# Revit family: BE_84840_de_DE
name_source: partatom
category: Leuchten
units: mm (PartAtom-declared; Revit-internal decimal feet)

## family parameters
Basisbauteil = Fläche
Beim Laden mit Abzugskörper schneiden = Ja
Bemaßung runder Anschluss = Durchmesser verwenden
Gemeinsam genutzt = Nein
Lichtquelle = Nein
Raumberechnungspunkt = Ja
Teiletyp = Normal

## types (2) — shared parameters
AC/DC = AC
Aktualisierung = 2022-05-19T04:00:07
Anschlussleitung = 5.0 m X05RN-F FEP 2 × 1² + 1G2,5²
BEGA_Dummy = Nein
BEGA_Intern = Ja
BEGA_Intern_Konstruktion = Ja
BEGA_Intern_an = Ja
BEGA_Intern_aus = Ja
Beschreibung = Flächenscheinwerfer BEGA UniLink
Beschreibung_Sonderanfertigung = Hier können Sie Informationen zur Sonderanfertigung eintragen.
CE_Konformität = ja
Energieeffizienzklasse = LED A++ - A
Farbwiedergabeindex = CRI > 90
Frequenz = 50-60 Hz
Gewicht = 1.8 kg
Hersteller = BEGA
Lampe = LED 17.6 W
Lastklassifizierung = Beleuchtung
Lebensdauerkriterien = L70B50 @ 25 °C = 200000 h
Logo = BEGA_Logo.png
M_G = Ja
Material_04 = BEGA_Kunststoff_Grafit_matt
Material_06 = BEGA_Oberfläche_Edelstahl_gebürstet
Material_09 = BEGA_Glas_klar
Material_15 = BEGA_Leuchtmedium_matt
Material_17 = BEGA_Reflektor
Produktdatenblatt = https://cdn.bega.com
Scheinlast = 0 VA
Schutzart = IP 65
Schutzklasse = I
Sonderanfertigung = Nein
Spannung = 240 V
Strom = 0,1 A
URL = https://www.bega.com
Umgebungstemperatur = 25 °C
zero-valued in all types: Vorgabe-Ansicht

## per-type parameters (varying)
| type | BEGA_IES1 | BEGA_IES2 | Bestellnummer | Farbtemperatur | LED_Modulbezeichnung | Lampenlichtstrom | Leuchtenlichtstrom | Modell |
| BEGA_84840_Grafit_K3 | Ja | Nein | 84840K3 | 3000 K | LED-0313/930 | 2780 lm | 2170 lm | 84840K3 |
| BEGA_84840_Grafit_K4 | Nein | Ja | 84840K4 | 4000 K | LED-0313/940 | 2940 lm | 2295 lm | 84840K4 |

## geometry (parser evidence)
native form markers: Blend x2, Sweep x16
no freeform markers — native parametric forms only
